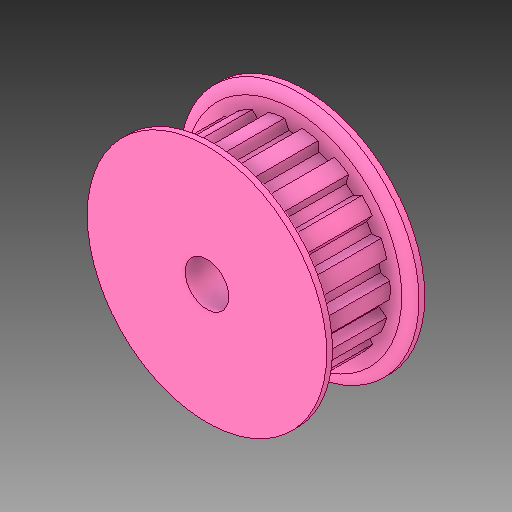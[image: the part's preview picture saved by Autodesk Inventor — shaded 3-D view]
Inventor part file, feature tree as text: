
AUTODESK INVENTOR PART (.ipt)
format: ipt  version: 2017 SP1 (Build 210196100, 196)  size: 248,832 bytes
history: native  units: in
note: dims shown in document units (in); Inventor stores cm internally (conversion verified against a paired STEP export)
features: extrude x2, sketch x2, projected_geometry x1, pattern_circular x1
ambient origin geometry x8: Origin, YZ Plane, XZ Plane, XY Plane, X Axis, Y Axis, Z Axis, Center Point
bodies: Solid1 (feature_tree)
feature tree (6):
  extrude  "Extrusion1"  Depth=1.0in
  extrude  "Extrusion2"  [1 undecoded]
  sketch  "Sketch1"  dims[d0=1.0in d1=0.0in d2=0.5in]
  projected_geometry  "Projected Loop1"
  sketch  "Sketch2"  dims[d3=1.0in d4=0.0in]
  pattern_circular  "CirPattern2"
note: 1 required parameter value undecoded (feature->parameter linkage not recoverable at this tier; creation-order binding heuristic only, values carry confidence <= 0.55)
